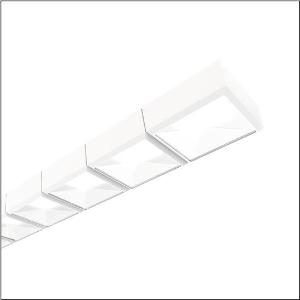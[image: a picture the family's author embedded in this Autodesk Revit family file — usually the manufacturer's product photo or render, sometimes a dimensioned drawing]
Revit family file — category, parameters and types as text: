
# Revit family: scriptus_r__11_5mz212d03wa_20e5
name_source: partatom
category: Lighting Fixtures
units: mm (PartAtom-declared; Revit-internal decimal feet)

## family parameters
Cut with Voids When Loaded = No
Host = Face
Light Source = No
Part Type = Normal
Room Calculation Point = No
Round Connector Dimension = Use Diameter
Shared = No

## types (1)
- Scriptus® 11 (1 x LED 3000K / CRI = 80 (unbekannt), 2200 lm, 3000K)
    Apparent Load = 35 VA
    CIE Flux Codes = 82 95 99 100 100
    Color Rendering = 80
    Color Temperature = 3000K
    Default Elevation = 1800 mm
    Description = Scriptus® 11, office luminaire, primary optical cover: lenses, CAT 2 (L<= 3000cd/m²), light emission: direct distribution, primary light characteristic: symmetric, installation type: surface-mounted, LED, rated luminous flux: 4.390lm, luminous efficacy: 127lm/W, light colour: 830, colour temperature: 3000K, control gear: ECG DALI, with terminal, 5-pole, mains connection: 230V, AC, 50Hz, rated input power: 35W, housing, luminaire housing, of aluminium, traffic white (RAL 9016), length: 1.658mm, width: 114mm, height: 57mm, protection rating (complete): IP20, insulation class (complete): insulation class I (protective earthing), certification: CE, ENEC, VDE, protection symbol: F, permissible operating ambient temperature: 0..+35°C, standard: EN 50419, packaging unit: 1 piece
    Height = 57 mm
    Lamp = 1 x LED 3000K / CRI >= 80 (unbekannt)
    Lamp Light Flux = 2200 lm
    Lamp count = 1
    Length = 1658 mm
    Luminous efficacy = 127 lm/W
    Manufacturer = Siteco
    ModVariant = No
    Model = 5MZ212D03WA
    Mounting Place = Ceiling
    Mounting Type = Surface mounted
    Number of Poles = 1
    OnlyDefault = Yes
    Power Factor = 1
    Product Name = Scriptus® 11
    Product group = office luminaire | ceiling mounted
    ProductGroupID = 300
    Protection Class = Protection class I
    Protection Degree = IP 20
    RLX_Detail_Level = 1
    RLX_Emergency_Light_Flux = 0 lm
    RLX_Emergency_Type = 0
    RLX_Emergency_Type_DB = No
    RlxData = <blob elided: 29489 chars, md5=296cc8e2>
    Socket = socket
    Standby Power = 0 W
    System Light Flux = 4400 lm
    System Power = 35 W
    Type Comments = Product without accessories
    Type Image = l_1004833.jpg
    URL = http://relux.com
    VarID = ---
    Voltage = 0 V
    Weight = 0.00 kg
    Width = 114 mm

## geometry (parser evidence)
native form markers: Blend x4, Sweep x15
no freeform markers — native parametric forms only
